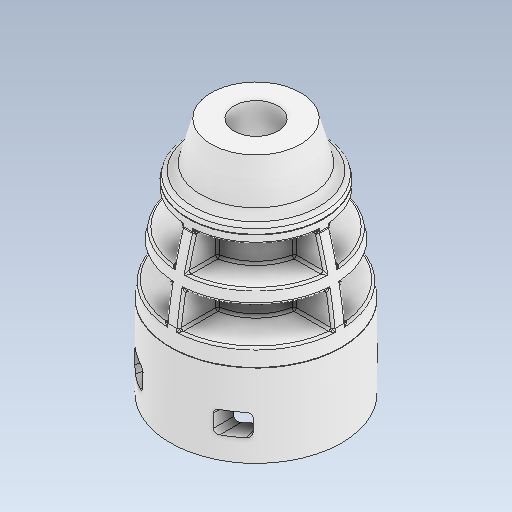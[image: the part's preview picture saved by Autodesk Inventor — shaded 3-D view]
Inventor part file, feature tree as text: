
AUTODESK INVENTOR PART (.ipt)
format: ipt  version: 2020 (Build 240168000, 168)  size: 837,632 bytes
history: native  units: in
note: dims shown in document units (in); Inventor stores cm internally (conversion verified against a paired STEP export)
features: fillet x1
ambient origin geometry x8: Origin, YZ Plane, XZ Plane, XY Plane, X Axis, Y Axis, Z Axis, Center Point
bodies: Solid1 (feature_tree)
feature tree (1):
  fillet  "Fillet3"  [1 undecoded]
note: 1 required parameter value undecoded (feature->parameter linkage not recoverable at this tier; creation-order binding heuristic only, values carry confidence <= 0.55)
